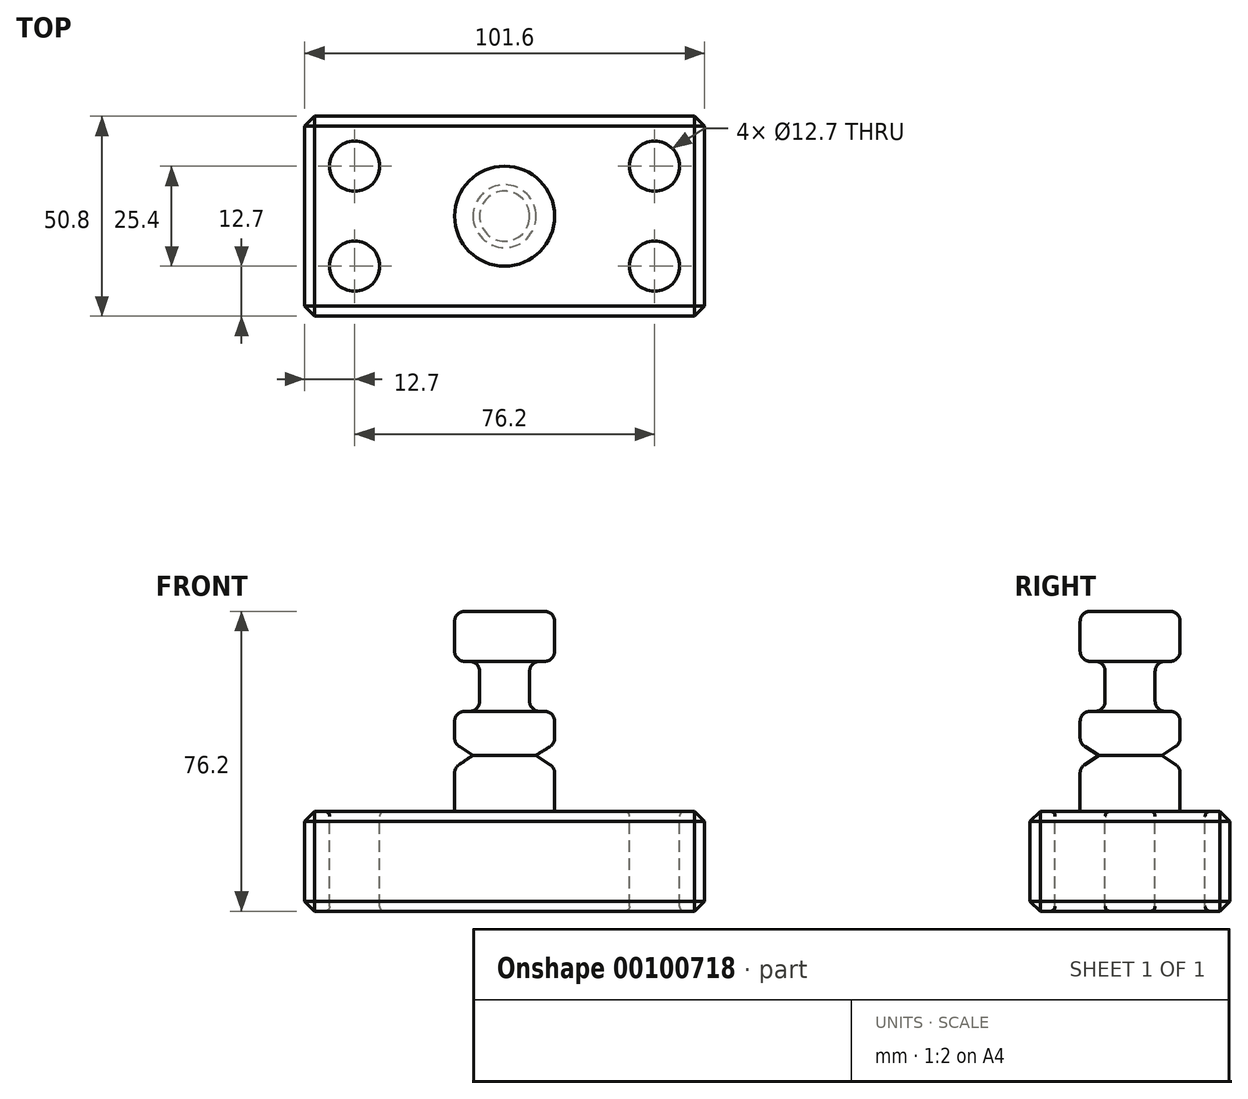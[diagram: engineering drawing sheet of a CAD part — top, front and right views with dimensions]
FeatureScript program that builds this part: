
annotation { "Feature Type Name" : "Feature", "Feature Type Description" : "" }
export const myFeature = defineFeature(function(context is Context, id is Id, definition is map)
    precondition{}
    {
        {
            var Q0;
            Q0=qCreatedBy(makeId("Top.planeOp"),FACE);
            var sketch = newSketch(context, id + "F0", { "sketchPlane" : qUnion([Q0])});
            skLineSegment(sketch, "E0.bottom", {"start": v(-50.8, 25.4) * mm, "end": v(50.8, 25.4) * mm});
            skLineSegment(sketch, "E0.top", {"start": v(-50.8, -25.4) * mm, "end": v(50.8, -25.4) * mm});
            skLineSegment(sketch, "E0.left", {"start": v(50.8, -25.4) * mm, "end": v(50.8, 25.4) * mm});
            skLineSegment(sketch, "E0.right", {"start": v(-50.8, -25.4) * mm, "end": v(-50.8, 25.4) * mm});
            skPoint(sketch, "E0.middle", {"position": v(0, 0) * mm});
            skSolve(sketch);
        }
        {
            var Q0;
            Q0=makeQuery(id+"F0.imprint","IMPRINT",FACE,{"disambiguationData":[TD([[makeQuery(id+"F0.imprint","IMPRINT",EDGE,{"derivedFrom":sQuery(id+"F0.wireOp",EDGE,"E0.bottom")}),-1.0]])]});
            extrude(context, id + "F1", {"entities" : qUnion([Q0]), "depth" : 25.4 * mm});
        }
        {
            var Q0;
            Q0=makeQuery(id+"F1.opExtrude","CAP_FACE",FACE,{"disambiguationData":[OSD([sQuery(id+"F0.wireOp",EDGE,"E0.bottom"),sQuery(id+"F0.wireOp",EDGE,"E0.top"),sQuery(id+"F0.wireOp",EDGE,"E0.left"),sQuery(id+"F0.wireOp",EDGE,"E0.right")])],"isStart":false});
            var sketch = newSketch(context, id + "F2", { "sketchPlane" : qUnion([Q0])});
            skCircle(sketch, "E1", {"center": v(-38.1, 12.7) * mm, "radius": 6.35 * mm});
            skCircle(sketch, "E2", {"center": v(-38.1, -12.7) * mm, "radius": 6.35 * mm});
            skCircle(sketch, "E3", {"center": v(38.1, -12.7) * mm, "radius": 6.35 * mm});
            skCircle(sketch, "E4", {"center": v(38.1, 12.7) * mm, "radius": 6.35 * mm});
            skSolve(sketch);
        }
        {
            var Q0;
            Q0 = qSketchRegion(id + "F2", true);
            extrude(context, id + "F3", {"entities" : qUnion([Q0]), "operationType" : NewBodyOperationType.REMOVE, "endBound" : BoundingType.THROUGH_ALL, "oppositeDirection" : true, "depth" : 25.4 * mm});
        }
        {
            var Q0;
            Q0=qCreatedBy(makeId("Front.planeOp"),FACE);
            var sketch = newSketch(context, id + "F4", { "sketchPlane" : qUnion([Q0])});
            skLineSegment(sketch, "E5.bottom", {"start": v(0, 76.2) * mm, "end": v(-12.7, 76.2) * mm});
            skLineSegment(sketch, "E5.top", {"start": v(0, 25.4) * mm, "end": v(-12.7, 25.4) * mm});
            skLineSegment(sketch, "E5.left", {"start": v(0, 76.2) * mm, "end": v(0, 25.4) * mm});
            skLineSegment(sketch, "E5.right", {"start": v(-12.7, 76.2) * mm, "end": v(-12.7, 25.4) * mm});
            skSolve(sketch);
        }
        {
            var Q0;
            Q0=makeQuery(id+"F4.imprint","IMPRINT",FACE,{"disambiguationData":[TD([[makeQuery(id+"F4.imprint","IMPRINT",EDGE,{"derivedFrom":sQuery(id+"F4.wireOp",EDGE,"E5.bottom")}),1.0]])]});
            var Q1;
            Q1=sQuery(id+"F4.wireOp",EDGE,"E5.left");
            revolve(context, id + "F5", {"operationType" : NewBodyOperationType.ADD, "entities" : qUnion([Q0]), "axis" : qUnion([Q1]), "revolveType" : RevolveType.FULL});
        }
        {
            var Q0;
            Q0=qCreatedBy(makeId("Front.planeOp"),FACE);
            var sketch = newSketch(context, id + "F6", { "sketchPlane" : qUnion([Q0])});
            skLineSegment(sketch, "E6.bottom", {"start": v(-6.35, 63.5) * mm, "end": v(-16.87, 63.5) * mm});
            skLineSegment(sketch, "E6.top", {"start": v(-6.35, 50.8) * mm, "end": v(-16.87, 50.8) * mm});
            skLineSegment(sketch, "E6.left", {"start": v(-6.35, 63.5) * mm, "end": v(-6.35, 50.8) * mm});
            skLineSegment(sketch, "E6.right", {"start": v(-16.87, 63.5) * mm, "end": v(-16.87, 50.8) * mm});
            skLineSegment(sketch, "E7", {"start": v(0, 0) * mm, "end": v(0, 84.99) * mm, "construction": true});
            skSolve(sketch);
        }
        {
            var Q0;
            Q0=makeQuery(id+"F6.imprint","IMPRINT",FACE,{"disambiguationData":[TD([[makeQuery(id+"F6.imprint","IMPRINT",EDGE,{"derivedFrom":sQuery(id+"F6.wireOp",EDGE,"E6.bottom")}),1.0]])]});
            var Q1;
            Q1=sQuery(id+"F6.wireOp",EDGE,"E7");
            revolve(context, id + "F7", {"operationType" : NewBodyOperationType.REMOVE, "entities" : qUnion([Q0]), "axis" : qUnion([Q1]), "revolveType" : RevolveType.FULL, "oppositeDirection" : true});
        }
        {
            var Q0;
            Q0=makeQuery(id+"F7.boolean.opBoolean","INTERSECT",EDGE,{"derivedFrom":[makeQuery(id+"F5.opRevolve","SWEPT_FACE",FACE,{"disambiguationData":[OSD([sQuery(id+"F4.wireOp",EDGE,"E5.right")])]}),makeQuery(id+"F7.opRevolve","SWEPT_FACE",FACE,{"disambiguationData":[OSD([sQuery(id+"F6.wireOp",EDGE,"E6.top")])]})]});
            var Q1;
            Q1=makeQuery(id+"F7.boolean.opBoolean","INTERSECT",EDGE,{"derivedFrom":[makeQuery(id+"F5.opRevolve","SWEPT_FACE",FACE,{"disambiguationData":[OSD([sQuery(id+"F4.wireOp",EDGE,"E5.right")])]}),makeQuery(id+"F7.opRevolve","SWEPT_FACE",FACE,{"disambiguationData":[OSD([sQuery(id+"F6.wireOp",EDGE,"E6.bottom")])]})]});
            var Q2;
            Q2=makeQuery(id+"F5.opRevolve","SWEPT_EDGE",EDGE,{"disambiguationData":[OSD([sQuery(id+"F4.wireOp",EDGE,"E5.top"),sQuery(id+"F4.wireOp",EDGE,"E5.right")])]});
            var Q3;
            Q3=makeQuery(id+"F5.opRevolve","SWEPT_EDGE",EDGE,{"disambiguationData":[OSD([sQuery(id+"F4.wireOp",EDGE,"E5.bottom"),sQuery(id+"F4.wireOp",EDGE,"E5.right")])]});
            var Q4;
            Q4=makeQuery(id+"F7.boolean.opBoolean","COPY",EDGE,{"derivedFrom":makeQuery(id+"F7.opRevolve","SWEPT_EDGE",EDGE,{"disambiguationData":[OSD([sQuery(id+"F6.wireOp",EDGE,"E6.top"),sQuery(id+"F6.wireOp",EDGE,"E6.left")])]})});
            var Q5;
            Q5=makeQuery(id+"F7.boolean.opBoolean","COPY",EDGE,{"derivedFrom":makeQuery(id+"F7.opRevolve","SWEPT_EDGE",EDGE,{"disambiguationData":[OSD([sQuery(id+"F6.wireOp",EDGE,"E6.bottom"),sQuery(id+"F6.wireOp",EDGE,"E6.left")])]})});
            fillet(context, id + "F8", {"entities" : qUnion([Q0, Q1, Q2, Q3, Q4, Q5]), "radius" : 2.54 * mm, "tangentPropagation" : true, "allowEdgeOverflow" : false});
        }
        {
            var Q0;
            Q0=makeQuery(id+"F1.opExtrude","CAP_EDGE",EDGE,{"disambiguationData":[OSD([sQuery(id+"F0.wireOp",EDGE,"E0.bottom")])],"isStart":false});
            var Q1;
            Q1=makeQuery(id+"F1.opExtrude","CAP_EDGE",EDGE,{"disambiguationData":[OSD([sQuery(id+"F0.wireOp",EDGE,"E0.left")])],"isStart":false});
            var Q2;
            Q2=makeQuery(id+"F1.opExtrude","SWEPT_FACE",FACE,{"disambiguationData":[OSD([sQuery(id+"F0.wireOp",EDGE,"E0.bottom")])]});
            var Q3;
            Q3=makeQuery(id+"F1.opExtrude","SWEPT_FACE",FACE,{"disambiguationData":[OSD([sQuery(id+"F0.wireOp",EDGE,"E0.left")])]});
            var Q4;
            Q4=makeQuery(id+"F1.opExtrude","SWEPT_FACE",FACE,{"disambiguationData":[OSD([sQuery(id+"F0.wireOp",EDGE,"E0.right")])]});
            var Q5;
            Q5=makeQuery(id+"F1.opExtrude","SWEPT_FACE",FACE,{"disambiguationData":[OSD([sQuery(id+"F0.wireOp",EDGE,"E0.top")])]});
            chamfer(context, id + "F9", {"entities" : qUnion([Q0, Q1, Q2, Q3, Q4, Q5]), "width" : 2.54 * mm, "tangentPropagation" : true});
        }
        {
            var Q0;
            Q0=makeQuery(id+"F3.boolean.opBoolean","COPY",FACE,{"derivedFrom":makeQuery(id+"F3.opExtrude","SWEPT_FACE",FACE,{"disambiguationData":[OSD([sQuery(id+"F2.wireOp",EDGE,"E1")])]})});
            var Q1;
            Q1=makeQuery(id+"F3.boolean.opBoolean","COPY",FACE,{"derivedFrom":makeQuery(id+"F3.opExtrude","SWEPT_FACE",FACE,{"disambiguationData":[OSD([sQuery(id+"F2.wireOp",EDGE,"E2")])]})});
            var Q2;
            Q2=makeQuery(id+"F3.boolean.opBoolean","COPY",FACE,{"derivedFrom":makeQuery(id+"F3.opExtrude","SWEPT_FACE",FACE,{"disambiguationData":[OSD([sQuery(id+"F2.wireOp",EDGE,"E3")])]})});
            var Q3;
            Q3=makeQuery(id+"F3.boolean.opBoolean","COPY",FACE,{"derivedFrom":makeQuery(id+"F3.opExtrude","SWEPT_FACE",FACE,{"disambiguationData":[OSD([sQuery(id+"F2.wireOp",EDGE,"E4")])]})});
            fillet(context, id + "F10", {"entities" : qUnion([Q0, Q1, Q2, Q3]), "radius" : 1.27 * mm, "tangentPropagation" : true, "allowEdgeOverflow" : false});
        }
        {
            var Q0;
            Q0=qCreatedBy(makeId("Front.planeOp"),FACE);
            var sketch = newSketch(context, id + "F11", { "sketchPlane" : qUnion([Q0])});
            skLineSegment(sketch, "E8", {"start": v(8, 39.66) * mm, "end": v(19.63, 46.91) * mm});
            skLineSegment(sketch, "E9", {"start": v(19.63, 46.91) * mm, "end": v(19.63, 31.8) * mm});
            skLineSegment(sketch, "E10", {"start": v(19.63, 31.8) * mm, "end": v(8, 39.66) * mm});
            skLineSegment(sketch, "E11", {"start": v(0, 0) * mm, "end": v(0, 61.95) * mm, "construction": true});
            skSolve(sketch);
        }
        {
            var Q0;
            Q0=makeQuery(id+"F11.imprint","IMPRINT",FACE,{"disambiguationData":[TD([[makeQuery(id+"F11.imprint","IMPRINT",EDGE,{"derivedFrom":sQuery(id+"F11.wireOp",EDGE,"E8")}),-1.0]])]});
            var Q1;
            Q1=sQuery(id+"F11.wireOp",EDGE,"E11");
            revolve(context, id + "F12", {"operationType" : NewBodyOperationType.REMOVE, "entities" : qUnion([Q0]), "axis" : qUnion([Q1]), "revolveType" : RevolveType.FULL, "oppositeDirection" : true});
        }
        {
            var Q0;
            Q0=makeQuery(id+"F12.boolean.opBoolean","INTERSECT",EDGE,{"derivedFrom":[makeQuery(id+"F7.boolean.opBoolean","SPLIT",FACE,{"disambiguationData":[TD([makeQuery(id+"F7.opRevolve","SWEPT_FACE",FACE,{"disambiguationData":[OSD([sQuery(id+"F6.wireOp",EDGE,"E6.top")])]})])],"derivedFrom":makeQuery(id+"F5.opRevolve","SWEPT_FACE",FACE,{"disambiguationData":[OSD([sQuery(id+"F4.wireOp",EDGE,"E5.right")])]})}),makeQuery(id+"F12.opRevolve","SWEPT_FACE",FACE,{"disambiguationData":[OSD([sQuery(id+"F11.wireOp",EDGE,"E8")])]})]});
            var Q1;
            Q1=makeQuery(id+"F12.boolean.opBoolean","INTERSECT",EDGE,{"derivedFrom":[makeQuery(id+"F7.boolean.opBoolean","SPLIT",FACE,{"disambiguationData":[TD([makeQuery(id+"F7.opRevolve","SWEPT_FACE",FACE,{"disambiguationData":[OSD([sQuery(id+"F6.wireOp",EDGE,"E6.top")])]})])],"derivedFrom":makeQuery(id+"F5.opRevolve","SWEPT_FACE",FACE,{"disambiguationData":[OSD([sQuery(id+"F4.wireOp",EDGE,"E5.right")])]})}),makeQuery(id+"F12.opRevolve","SWEPT_FACE",FACE,{"disambiguationData":[OSD([sQuery(id+"F11.wireOp",EDGE,"E10")])]})]});
            fillet(context, id + "F13", {"entities" : qUnion([Q0, Q1]), "radius" : 2.54 * mm, "tangentPropagation" : true, "allowEdgeOverflow" : false});
        }
    });
